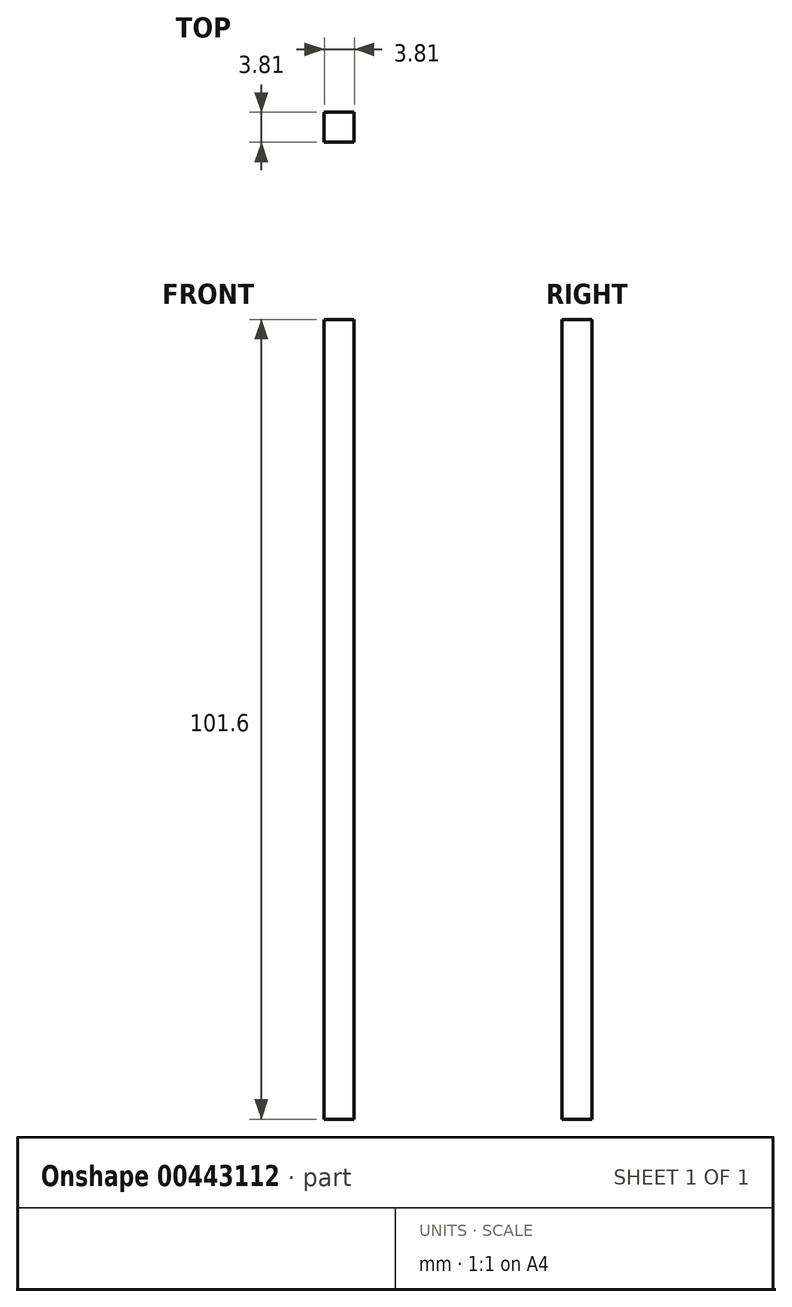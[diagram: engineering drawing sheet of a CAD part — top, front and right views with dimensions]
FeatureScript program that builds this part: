
annotation { "Feature Type Name" : "Feature", "Feature Type Description" : "" }
export const myFeature = defineFeature(function(context is Context, id is Id, definition is map)
    precondition{}
    {
        {
            var Q0;
            Q0=qCreatedBy(makeId("Front.planeOp"),FACE);
            var sketch = newSketch(context, id + "F0", { "sketchPlane" : qUnion([Q0])});
            skLineSegment(sketch, "E0.bottom", {"start": v(-105.66, 101.6) * mm, "end": v(-101.85, 101.6) * mm});
            skLineSegment(sketch, "E0.top", {"start": v(-105.66, 0) * mm, "end": v(-101.85, 0) * mm});
            skLineSegment(sketch, "E0.left", {"start": v(-105.66, 101.6) * mm, "end": v(-105.66, 0) * mm});
            skLineSegment(sketch, "E0.right", {"start": v(-101.85, 101.6) * mm, "end": v(-101.85, 0) * mm});
            skSolve(sketch);
        }
        {
            var Q0;
            Q0=makeQuery(id+"F0.imprint","IMPRINT",FACE,{"disambiguationData":[TD([[makeQuery(id+"F0.imprint","IMPRINT",EDGE,{"derivedFrom":sQuery(id+"F0.wireOp",EDGE,"E0.bottom")}),-1.0]])]});
            extrude(context, id + "F1", {"entities" : qUnion([Q0]), "depth" : 3.8 * mm, "offsetDistance" : 25.4 * mm});
        }
    });
